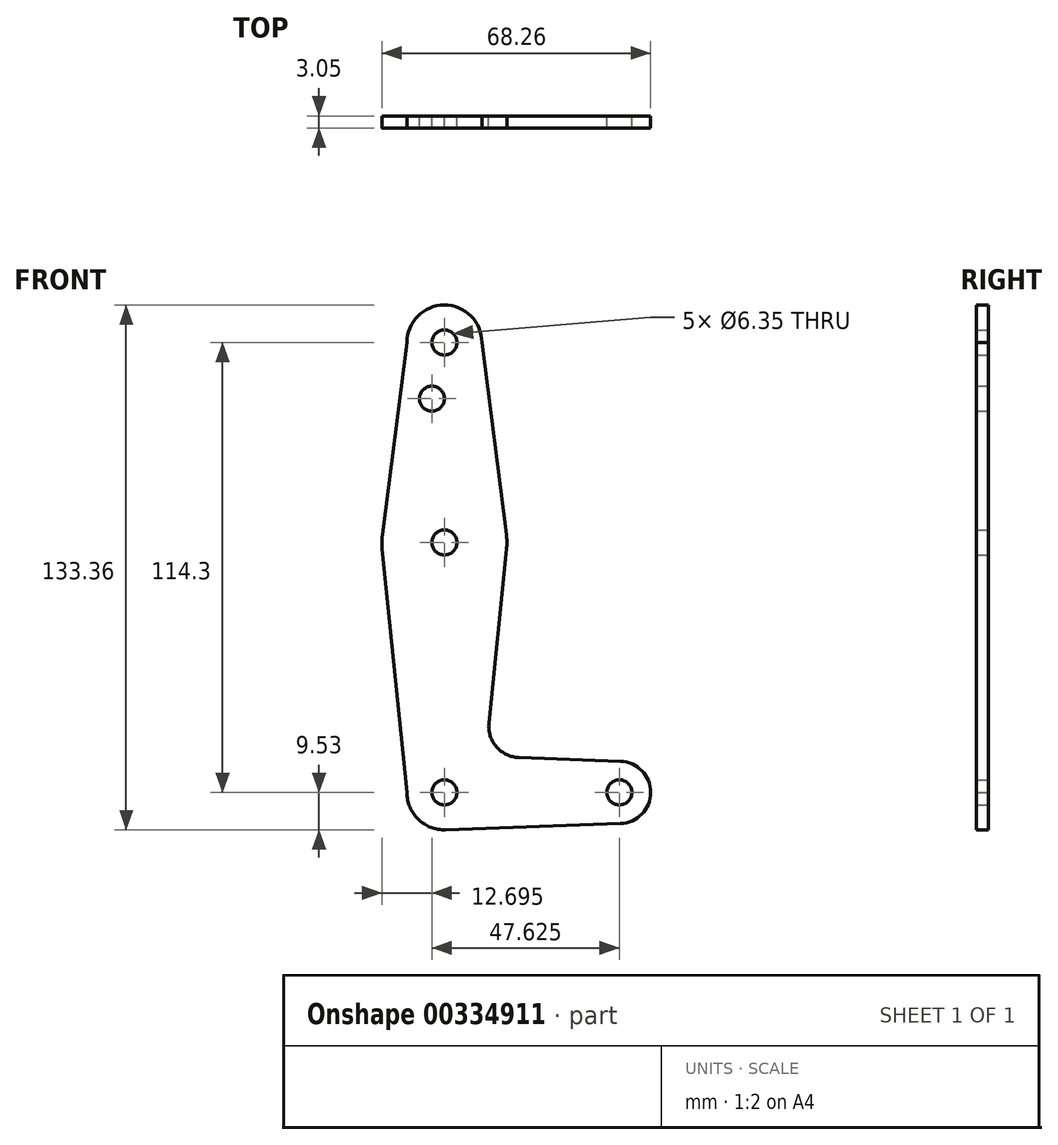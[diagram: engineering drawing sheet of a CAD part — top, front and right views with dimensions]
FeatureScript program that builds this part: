
annotation { "Feature Type Name" : "Feature", "Feature Type Description" : "" }
export const myFeature = defineFeature(function(context is Context, id is Id, definition is map)
    precondition{}
    {
        {
            var Q0;
            Q0=qCreatedBy(makeId("Front.planeOp"),FACE);
            var sketch = newSketch(context, id + "F0", { "sketchPlane" : qUnion([Q0])});
            skLineSegment(sketch, "E0", {"start": v(0, 0) * mm, "end": v(44.45, 0) * mm});
            skCircle(sketch, "E1", {"center": v(44.45, 0) * mm, "radius": 7.94 * mm});
            skLineSegment(sketch, "E2", {"start": v(0, 0) * mm, "end": v(0, 114.3) * mm});
            skLineSegment(sketch, "E3", {"start": v(18.93, 8.85) * mm, "end": v(44.73, 7.93) * mm});
            skLineSegment(sketch, "E4", {"start": v(0, -9.53) * mm, "end": v(44.73, -7.93) * mm});
            skCircle(sketch, "E5", {"center": v(0, 114.3) * mm, "radius": 9.53 * mm});
            skCircle(sketch, "E6", {"center": v(0, 63.5) * mm, "radius": 15.88 * mm});
            skCircle(sketch, "E7", {"center": v(0, 0) * mm, "radius": 9.53 * mm});
            skLineSegment(sketch, "E8", {"start": v(-9.52, 0) * mm, "end": v(-15.8, 61.9) * mm});
            skLineSegment(sketch, "E9", {"start": v(11.3, 17.6) * mm, "end": v(15.8, 61.9) * mm});
            skLineSegment(sketch, "E10", {"start": v(-9.52, 114.3) * mm, "end": v(-15.8, 65.14) * mm});
            skLineSegment(sketch, "E11", {"start": v(9.52, 114.3) * mm, "end": v(15.8, 65.14) * mm});
            skCircle(sketch, "E12", {"center": v(0, 114.3) * mm, "radius": 3.18 * mm});
            skCircle(sketch, "E13", {"center": v(0, 63.5) * mm, "radius": 3.18 * mm});
            skCircle(sketch, "E14", {"center": v(0, 0) * mm, "radius": 3.18 * mm});
            skCircle(sketch, "E15", {"center": v(44.45, 0) * mm, "radius": 3.18 * mm});
            skCircle(sketch, "E16", {"center": v(-3.18, 100.03) * mm, "radius": 3.18 * mm});
            skArc(sketch, "E17.filletArc", {"start": v(11.3, 17.6) * mm, "mid": v(13.22, 11.57) * mm, "end": v(18.93, 8.85) * mm});
            skSolve(sketch);
        }
        {
            var Q0;
            Q0 = qSketchRegion(id + "F0", true);
            var Q1;
            {var subQ0=sQuery(id+"F0.wireOp",EDGE,"E14");var subQ1=sQuery(id+"F0.wireOp",EDGE,"E0");var subQ2=makeQuery(id+"F0.imprint","INTERSECT",VERTEX,{"derivedFrom":[subQ1,subQ0]});Q1=makeQuery(id+"F0.imprint","IMPRINT",FACE,{"disambiguationData":[TD([[makeQuery(id+"F0.imprint","IMPRINT",EDGE,{"disambiguationData":[TD([[subQ2,-1.0]])],"derivedFrom":subQ1}),1.0]])]});}
            extrude(context, id + "F1", {"entities" : qUnion([Q0, Q1]), "depth" : 3.05 * mm});
        }
    });
